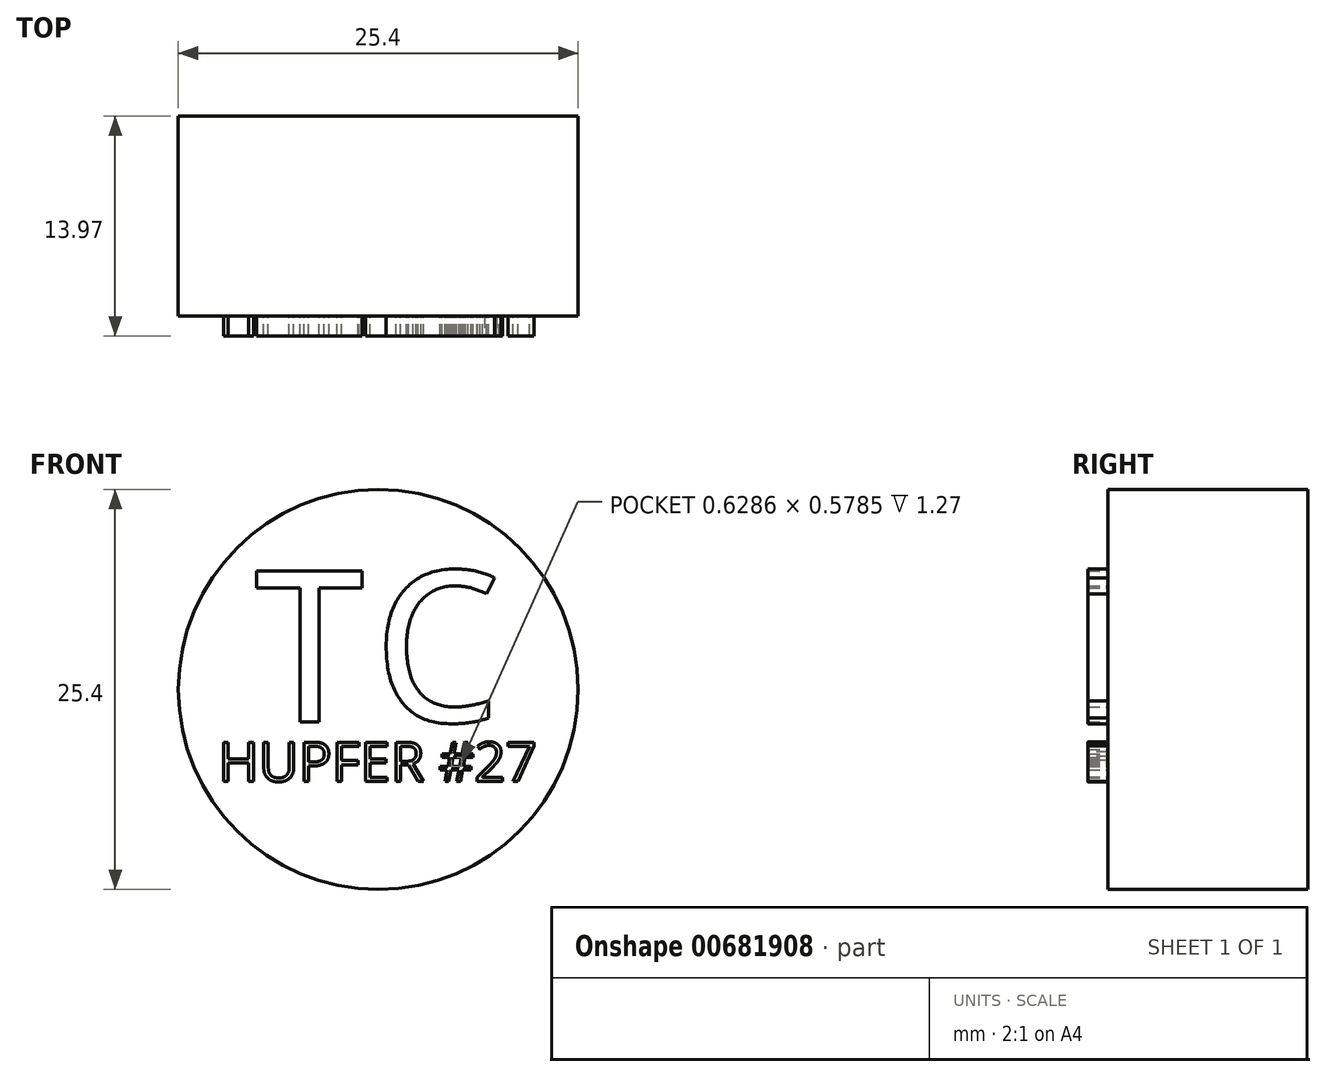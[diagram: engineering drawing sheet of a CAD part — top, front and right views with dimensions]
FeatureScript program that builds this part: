
annotation { "Feature Type Name" : "Feature", "Feature Type Description" : "" }
export const myFeature = defineFeature(function(context is Context, id is Id, definition is map)
    precondition{}
    {
        {
            var Q0;
            Q0=qCreatedBy(makeId("Front.planeOp"),FACE);
            var sketch = newSketch(context, id + "F0", { "sketchPlane" : qUnion([Q0])});
            skCircle(sketch, "E0", {"center": v(-44.07, 49.18) * mm, "radius": 12.7 * mm});
            skSolve(sketch);
        }
        {
            var Q0;
            Q0 = qSketchRegion(id + "F0", true);
            extrude(context, id + "F1", {"entities" : qUnion([Q0]), "depth" : 12.7 * mm, "offsetDistance" : 25.4 * mm});
        }
        {
            var Q0;
            Q0=makeQuery(id+"F1.opExtrude","CAP_FACE",FACE,{"disambiguationData":[OSD([sQuery(id+"F0.wireOp",EDGE,"E0")])],"isStart":false});
            var sketch = newSketch(context, id + "F2", { "sketchPlane" : qUnion([Q0])});
            skText(sketch, "E1", { "text": "TC", "fontName": "DroidSansMono.ttf"});
            const initialGuessF2  = {"E1": [-0.05245, 0.04713, 1, 0, 0.00965]};
            skSetInitialGuess(sketch, initialGuessF2);
            skSolve(sketch);
        }
        {
            var Q0;
            Q0 = qSketchRegion(id + "F2", true);
            extrude(context, id + "F3", {"entities" : qUnion([Q0]), "operationType" : NewBodyOperationType.ADD, "depth" : 1.27 * mm, "offsetDistance" : 25.4 * mm});
        }
        {
            var Q0;
            Q0=makeQuery(id+"F1.opExtrude","CAP_FACE",FACE,{"disambiguationData":[OSD([sQuery(id+"F0.wireOp",EDGE,"E0")])],"isStart":false});
            var sketch = newSketch(context, id + "F4", { "sketchPlane" : qUnion([Q0])});
            skText(sketch, "E2", { "text": "HUPFER #27", "fontName": "OpenSans-Regular.ttf"});
            const initialGuessF4  = {"E2": [-0.05423, 0.04334, 1, 0, 0.00251]};
            skSetInitialGuess(sketch, initialGuessF4);
            skSolve(sketch);
        }
        {
            var Q0;
            Q0 = qSketchRegion(id + "F4", true);
            extrude(context, id + "F5", {"entities" : qUnion([Q0]), "operationType" : NewBodyOperationType.ADD, "depth" : 1.27 * mm, "offsetDistance" : 25.4 * mm});
        }
    });
